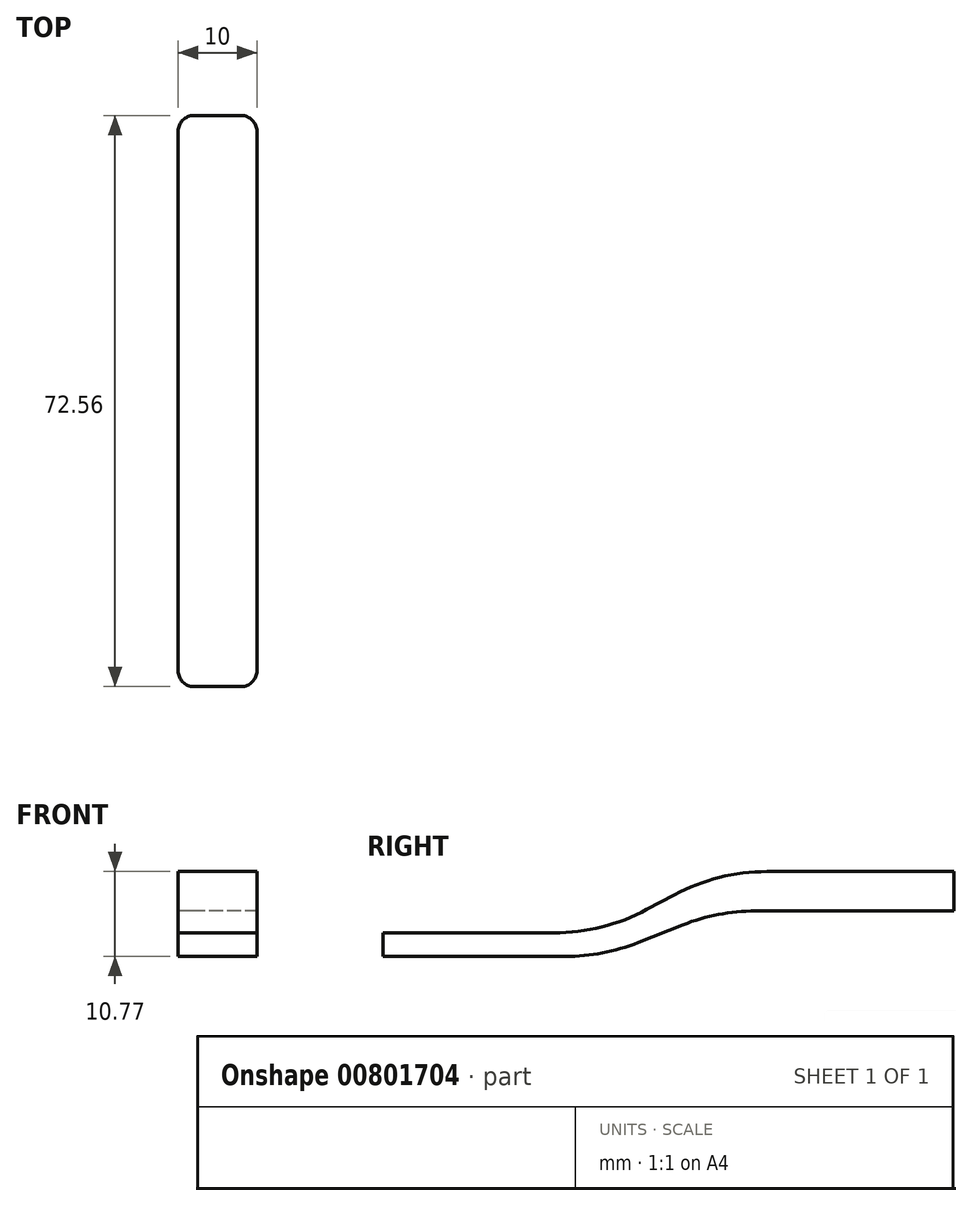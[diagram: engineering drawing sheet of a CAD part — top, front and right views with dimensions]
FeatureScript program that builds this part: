
annotation { "Feature Type Name" : "Feature", "Feature Type Description" : "" }
export const myFeature = defineFeature(function(context is Context, id is Id, definition is map)
    precondition{}
    {
        {
            var Q0;
            Q0=qCreatedBy(makeId("Right.planeOp"),FACE);
            var sketch = newSketch(context, id + "F0", { "sketchPlane" : qUnion([Q0])});
            skLineSegment(sketch, "E0.bottom", {"start": v(0, 0) * mm, "end": v(20, 0) * mm});
            skLineSegment(sketch, "E0.top", {"start": v(0, 3) * mm, "end": v(20, 3) * mm});
            skLineSegment(sketch, "E0.right", {"start": v(20, 0) * mm, "end": v(20, 3) * mm});
            skLineSegment(sketch, "E1.bottom", {"start": v(34.56, 10.77) * mm, "end": v(64.56, 10.77) * mm});
            skLineSegment(sketch, "E1.top", {"start": v(34.56, 5.77) * mm, "end": v(64.56, 5.77) * mm});
            skLineSegment(sketch, "E1.left", {"start": v(34.56, 10.77) * mm, "end": v(34.56, 5.77) * mm});
            skLineSegment(sketch, "E1.right", {"start": v(64.56, 10.77) * mm, "end": v(64.56, 5.77) * mm});
            skLineSegment(sketch, "E2", {"start": v(34.56, 10.77) * mm, "end": v(20, 3) * mm});
            skLineSegment(sketch, "E3", {"start": v(20, 0) * mm, "end": v(34.56, 5.77) * mm});
            skLineSegment(sketch, "E4", {"start": v(0, 3) * mm, "end": v(-8, 3) * mm});
            skLineSegment(sketch, "E5", {"start": v(-8, 3) * mm, "end": v(-8, 0) * mm});
            skLineSegment(sketch, "E6", {"start": v(-8, 0) * mm, "end": v(0, 0) * mm});
            skSolve(sketch);
        }
        {
            var Q0;
            Q0=makeQuery(id+"F0.imprint","IMPRINT",FACE,{"disambiguationData":[TD([[makeQuery(id+"F0.imprint","IMPRINT",EDGE,{"derivedFrom":sQuery(id+"F0.wireOp",EDGE,"E0.bottom")}),1.0]])]});
            var Q1;
            Q1=makeQuery(id+"F0.imprint","IMPRINT",FACE,{"disambiguationData":[TD([[makeQuery(id+"F0.imprint","IMPRINT",EDGE,{"derivedFrom":sQuery(id+"F0.wireOp",EDGE,"E0.right")}),-1.0]])]});
            var Q2;
            Q2=makeQuery(id+"F0.imprint","IMPRINT",FACE,{"disambiguationData":[TD([[makeQuery(id+"F0.imprint","IMPRINT",EDGE,{"derivedFrom":sQuery(id+"F0.wireOp",EDGE,"E1.bottom")}),-1.0]])]});
            extrude(context, id + "F1", {"entities" : qUnion([Q0, Q1, Q2]), "endBound" : BoundingType.SYMMETRIC, "depth" : 10 * mm, "offsetDistance" : 25 * mm});
        }
        {
            var Q0;
            Q0=makeQuery(id+"F1.opExtrude","SWEPT_EDGE",EDGE,{"disambiguationData":[OSD([sQuery(id+"F0.wireOp",EDGE,"E0.top"),sQuery(id+"F0.wireOp",EDGE,"E0.right"),sQuery(id+"F0.wireOp",EDGE,"E2")])]});
            var Q1;
            Q1=makeQuery(id+"F1.opExtrude","SWEPT_EDGE",EDGE,{"disambiguationData":[OSD([sQuery(id+"F0.wireOp",EDGE,"E1.bottom"),sQuery(id+"F0.wireOp",EDGE,"E1.left"),sQuery(id+"F0.wireOp",EDGE,"E2")])]});
            var Q2;
            Q2=makeQuery(id+"F1.opExtrude","SWEPT_EDGE",EDGE,{"disambiguationData":[OSD([sQuery(id+"F0.wireOp",EDGE,"E1.top"),sQuery(id+"F0.wireOp",EDGE,"E1.left"),sQuery(id+"F0.wireOp",EDGE,"E3")])]});
            var Q3;
            Q3=makeQuery(id+"F1.opExtrude","SWEPT_EDGE",EDGE,{"disambiguationData":[OSD([sQuery(id+"F0.wireOp",EDGE,"E0.bottom"),sQuery(id+"F0.wireOp",EDGE,"E0.right"),sQuery(id+"F0.wireOp",EDGE,"E3")])]});
            fillet(context, id + "F2", {"entities" : qUnion([Q0, Q1, Q2, Q3]), "radius" : 25 * mm, "tangentPropagation" : true, "allowEdgeOverflow" : false});
        }
        {
            var Q0;
            Q0=makeQuery(id+"F1.opExtrude","CAP_EDGE",EDGE,{"disambiguationData":[OSD([sQuery(id+"F0.wireOp",EDGE,"E0.left")])],"isStart":false});
            var Q1;
            Q1=makeQuery(id+"F1.opExtrude","CAP_EDGE",EDGE,{"disambiguationData":[OSD([sQuery(id+"F0.wireOp",EDGE,"E0.left")])],"isStart":true});
            var Q2;
            Q2=makeQuery(id+"F1.opExtrude","CAP_EDGE",EDGE,{"disambiguationData":[OSD([sQuery(id+"F0.wireOp",EDGE,"E1.right")])],"isStart":false});
            var Q3;
            Q3=makeQuery(id+"F1.opExtrude","CAP_EDGE",EDGE,{"disambiguationData":[OSD([sQuery(id+"F0.wireOp",EDGE,"E1.right")])],"isStart":true});
            var Q4;
            Q4=makeQuery(id+"F1.opExtrude","CAP_EDGE",EDGE,{"disambiguationData":[OSD([sQuery(id+"F0.wireOp",EDGE,"E5")])],"isStart":false});
            var Q5;
            Q5=makeQuery(id+"F1.opExtrude","CAP_EDGE",EDGE,{"disambiguationData":[OSD([sQuery(id+"F0.wireOp",EDGE,"E5")])],"isStart":true});
            fillet(context, id + "F3", {"entities" : qUnion([Q0, Q1, Q2, Q3, Q4, Q5]), "radius" : 2 * mm, "tangentPropagation" : true, "allowEdgeOverflow" : false});
        }
    });
